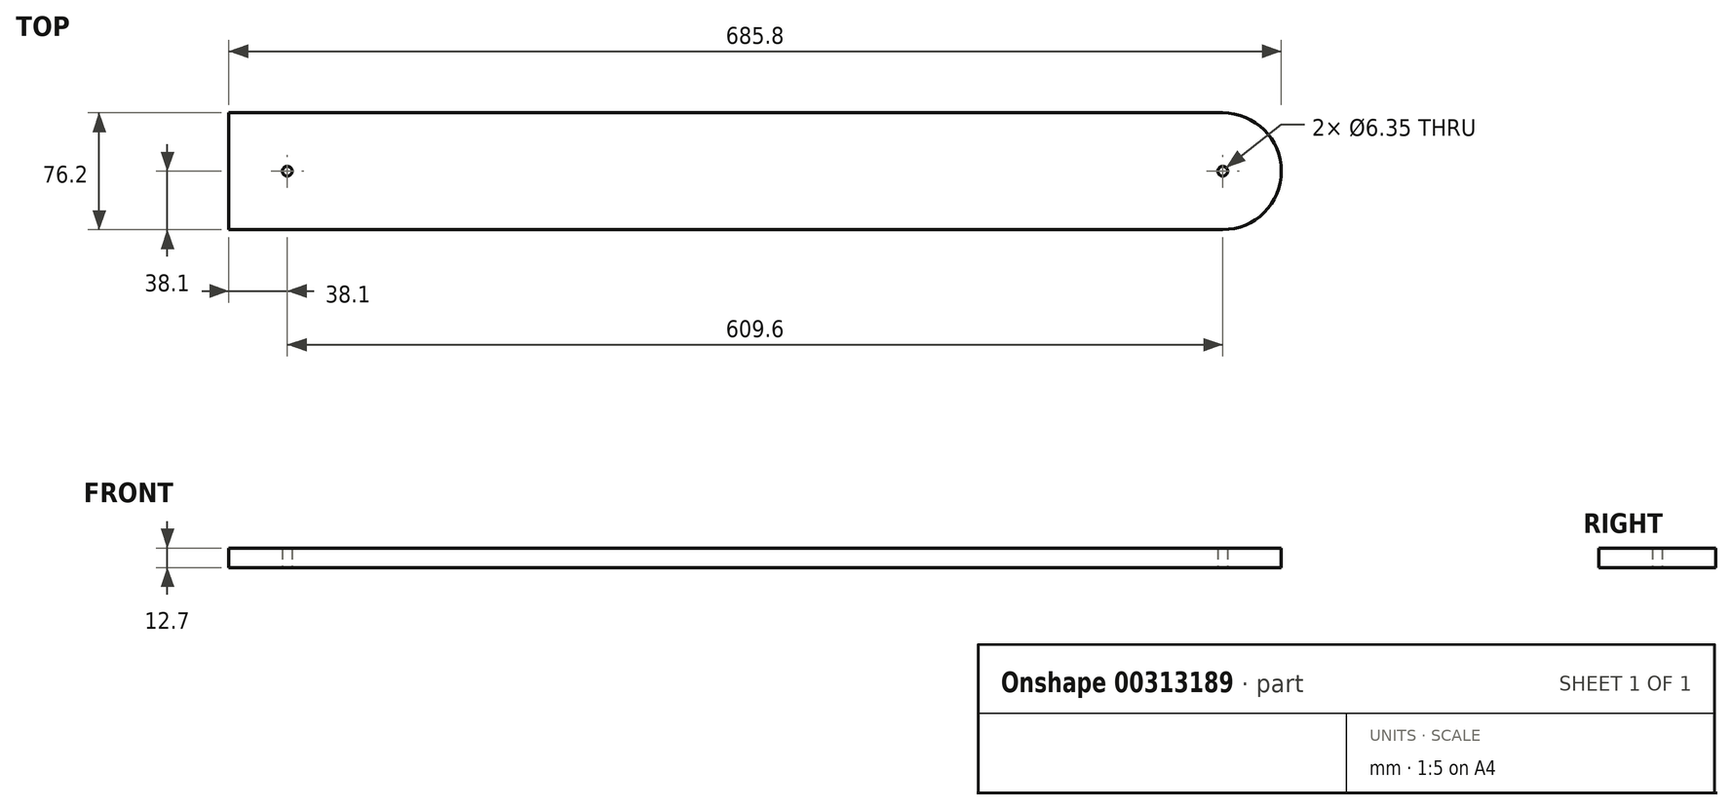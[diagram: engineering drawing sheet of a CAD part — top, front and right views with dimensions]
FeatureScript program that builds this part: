
annotation { "Feature Type Name" : "Feature", "Feature Type Description" : "" }
export const myFeature = defineFeature(function(context is Context, id is Id, definition is map)
    precondition{}
    {
        {
            var Q0;
            Q0=qCreatedBy(makeId("Top.planeOp"),FACE);
            var sketch = newSketch(context, id + "F0", { "sketchPlane" : qUnion([Q0])});
            skLineSegment(sketch, "E0.bottom", {"start": v(-342.9, -38.1) * mm, "end": v(304.8, -38.1) * mm});
            skLineSegment(sketch, "E0.top", {"start": v(-342.9, 38.1) * mm, "end": v(304.8, 38.1) * mm});
            skLineSegment(sketch, "E0.left", {"start": v(-342.9, -38.1) * mm, "end": v(-342.9, 38.1) * mm});
            skPoint(sketch, "E0.middle", {"position": v(0, 0) * mm});
            skCircle(sketch, "E1", {"center": v(-304.8, 0) * mm, "radius": 3.18 * mm});
            skCircle(sketch, "E2", {"center": v(304.8, 0) * mm, "radius": 3.18 * mm});
            skArc(sketch, "E3", {"start": v(304.8, -38.1) * mm, "mid": v(342.9, 0) * mm, "end": v(304.8, 38.1) * mm});
            skPoint(sketch, "E4.orphan", {"position": v(342.9, 38.1) * mm});
            skPoint(sketch, "E5.orphan", {"position": v(342.9, -38.1) * mm});
            skPoint(sketch, "E6", {"position": v(342.9, 0) * mm});
            skSolve(sketch);
        }
        {
            var Q0;
            Q0=makeQuery(id+"F0.imprint","IMPRINT",FACE,{"disambiguationData":[TD([[makeQuery(id+"F0.imprint","IMPRINT",EDGE,{"derivedFrom":sQuery(id+"F0.wireOp",EDGE,"E0.bottom")}),1.0]])]});
            extrude(context, id + "F1", {"entities" : qUnion([Q0]), "depth" : 12.7 * mm});
        }
    });
